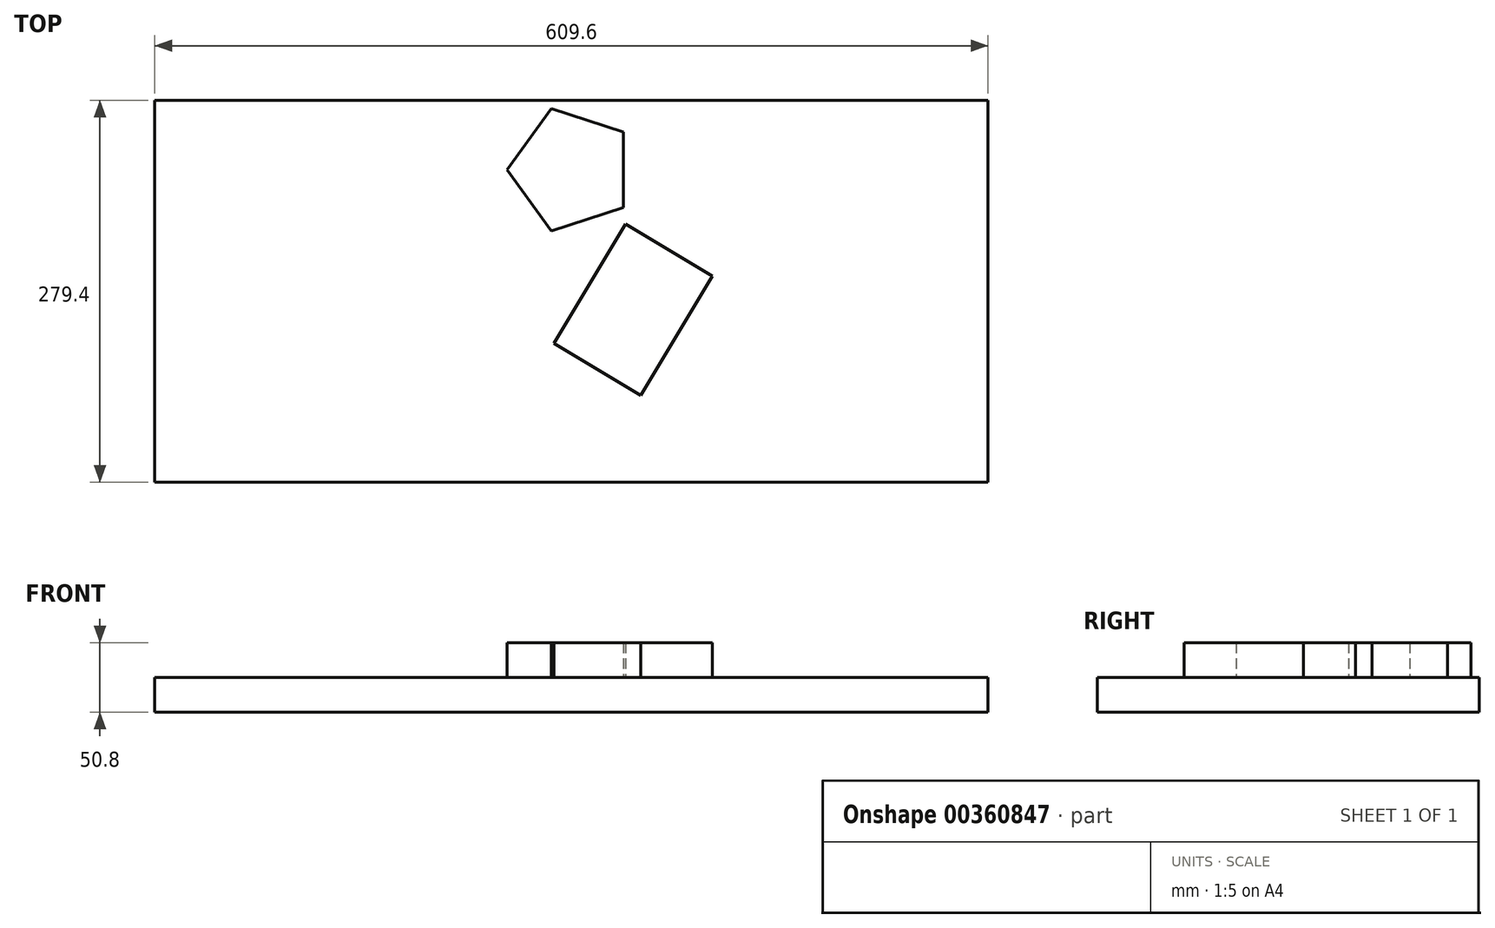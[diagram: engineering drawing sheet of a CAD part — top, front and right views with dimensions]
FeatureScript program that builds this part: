
annotation { "Feature Type Name" : "Feature", "Feature Type Description" : "" }
export const myFeature = defineFeature(function(context is Context, id is Id, definition is map)
    precondition{}
    {
        {
            var Q0;
            Q0=qCreatedBy(makeId("Top.planeOp"),FACE);
            var sketch = newSketch(context, id + "F0", { "sketchPlane" : qUnion([Q0])});
            skLineSegment(sketch, "E0.bottom", {"start": v(304.8, 228.6) * mm, "end": v(-304.8, 228.6) * mm});
            skLineSegment(sketch, "E0.top", {"start": v(304.8, -228.6) * mm, "end": v(-304.8, -228.6) * mm});
            skLineSegment(sketch, "E0.left", {"start": v(304.8, 228.6) * mm, "end": v(304.8, -228.6) * mm});
            skLineSegment(sketch, "E0.right", {"start": v(-304.8, 228.6) * mm, "end": v(-304.8, -228.6) * mm});
            skPoint(sketch, "E0.middle", {"position": v(0, 0) * mm});
            skSolve(sketch);
        }
        {
            var Q0;
            Q0=qSketchRegion(id+"F0",true);
            extrude(context, id + "F1", {"entities" : qUnion([Q0]), "depth" : 25.4 * mm});
        }
        {
            var Q0;
            Q0=makeQuery(id+"F1.opExtrude","CAP_FACE",FACE,{"disambiguationData":[OSD([sQuery(id+"F0.wireOp",EDGE,"E0.bottom"),sQuery(id+"F0.wireOp",EDGE,"E0.top"),sQuery(id+"F0.wireOp",EDGE,"E0.left"),sQuery(id+"F0.wireOp",EDGE,"E0.right")])],"isStart":false});
            var sketch = newSketch(context, id + "F2", { "sketchPlane" : qUnion([Q0])});
            skLineSegment(sketch, "E1.bottom", {"start": v(50.8, -165.1) * mm, "end": v(103.07, -77.98) * mm});
            skLineSegment(sketch, "E1.top", {"start": v(-12.7, -127) * mm, "end": v(39.57, -39.88) * mm});
            skLineSegment(sketch, "E1.left", {"start": v(50.8, -165.1) * mm, "end": v(-12.7, -127) * mm});
            skLineSegment(sketch, "E1.right", {"start": v(103.07, -77.98) * mm, "end": v(39.57, -39.88) * mm});
            skPoint(sketch, "E2", {"position": v(13.44, -83.44) * mm});
            skPoint(sketch, "E3", {"position": v(76.94, -121.54) * mm});
            skPoint(sketch, "E4", {"position": v(71.32, -58.93) * mm});
            skCircle(sketch, "E5.cCircle", {"center": v(0, 0) * mm, "radius": 38.1 * mm, "construction": true});
            skLineSegment(sketch, "E5.0", {"start": v(38.1, 27.68) * mm, "end": v(38.1, -27.68) * mm});
            skLineSegment(sketch, "E5.1", {"start": v(38.1, -27.68) * mm, "end": v(-14.55, -44.79) * mm});
            skLineSegment(sketch, "E5.2", {"start": v(-14.55, -44.79) * mm, "end": v(-47.1, 0) * mm});
            skLineSegment(sketch, "E5.3", {"start": v(-47.1, 0) * mm, "end": v(-14.55, 44.79) * mm});
            skLineSegment(sketch, "E5.4", {"start": v(-14.55, 44.79) * mm, "end": v(38.1, 27.68) * mm});
            skPoint(sketch, "E5.0.midPoint", {"position": v(38.1, 0) * mm});
            skPoint(sketch, "E6", {"position": v(19.05, -146.05) * mm});
            skPoint(sketch, "E7", {"position": v(46.8, -104.28) * mm});
            skSolve(sketch);
        }
        {
            var Q0;
            Q0=qSketchRegion(id+"F2",true);
            extrude(context, id + "F3", {"entities" : qUnion([Q0]), "depth" : 25.4 * mm});
        }
        {
            var Q0;
            Q0=makeQuery(id+"F1.opExtrude","SWEPT_FACE",FACE,{"disambiguationData":[OSD([sQuery(id+"F0.wireOp",EDGE,"E0.left")])]});
            var sketch = newSketch(context, id + "F4", { "sketchPlane" : qUnion([Q0])});
            skLineSegment(sketch, "E8.bottom", {"start": v(228.6, 0) * mm, "end": v(50.8, 0) * mm});
            skLineSegment(sketch, "E8.top", {"start": v(228.6, 25.4) * mm, "end": v(50.8, 25.4) * mm});
            skLineSegment(sketch, "E8.left", {"start": v(228.6, 0) * mm, "end": v(228.6, 25.4) * mm});
            skLineSegment(sketch, "E8.right", {"start": v(50.8, 0) * mm, "end": v(50.8, 25.4) * mm});
            skSolve(sketch);
        }
        {
            var Q0;
            Q0 = qSketchRegion(id + "F4", true);
            extrude(context, id + "F5", {"entities" : qUnion([Q0]), "operationType" : NewBodyOperationType.REMOVE, "endBound" : BoundingType.THROUGH_ALL, "oppositeDirection" : true, "depth" : 25.4 * mm});
        }
    });
